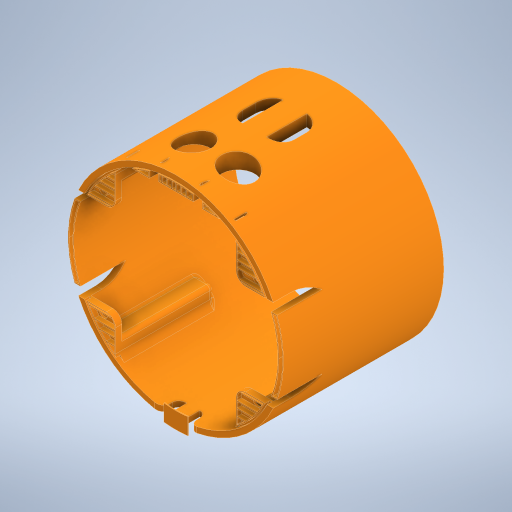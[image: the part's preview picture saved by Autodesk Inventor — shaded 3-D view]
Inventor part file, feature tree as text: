
AUTODESK INVENTOR PART (.ipt)
format: ipt  version: 2023 (Build 270158000, 158)  size: 1,089,536 bytes
history: native  units: mm
features: extrude x19, projected_geometry x15, sketch x13, fillet x10, mirror x5, plane x3, other x1
ambient origin geometry x8: Origin, YZ Plane, XZ Plane, XY Plane, X Axis, Y Axis, Z Axis, Center Point
bodies: Body1 (feature_tree)
feature tree (66):
  other  "Sólido1"
  extrude  "Extrusión1"  Depth=3.0mm
  extrude  "Extrusión2"  Depth=18.0mm
  extrude  "Extrusión3"  Depth=9.0mm
  extrude  "Extrusión4"  Depth=2.5mm TaperAngle=0.0deg
  sketch  "Boceto3"  dims[d3=50.0mm d4=18.0mm]
  extrude  "Extrusión5"  Depth=7.0mm TaperAngle=0.0deg
  fillet  "Empalme1"  Radius=7.0mm
  fillet  "Empalme2"  Radius=25.0mm
  fillet  "Empalme3"  Radius=53.0mm
  fillet  "Empalme4"  Radius=25.0mm
  fillet  "Empalme5"  Radius=1.0mm
  fillet  "Empalme6"  Radius=20.0mm
  fillet  "Empalme7"  Radius=4.0mm
  fillet  "Empalme8"  Radius=4.0mm
  sketch  "Boceto4"  dims[d5=4.5mm d8=9.0mm]
  extrude  "Extrusión6"  Depth=5.0mm
  extrude  "Extrusión7"  Depth=5.0mm
  extrude  "Extrusión8"  Depth=12.5mm
  sketch  "Boceto5"  dims[d9=15.0mm d10=2.5mm d11=0.0mm]
  extrude  "Extrusión9"  Depth=45.0mm
  fillet  "Empalme9"  Radius=2.0mm
  extrude  "Extrusión10"  Depth=18.0mm
  extrude  "Extrusión11"  Depth=2.5mm TaperAngle=0.0deg
  extrude  "Extrusión12"  Depth=35.0mm TaperAngle=0.0deg
  extrude  "Extrusión13"  Depth=10.0mm
  extrude  "Extrusión14"  Depth=10.0mm
  mirror  "Simetría1"
  mirror  "Simetría2"
  extrude  "Extrusión15"  Depth=10.0mm TaperAngle=0.0deg
  extrude  "Extrusión16"  Depth=10.0mm
  extrude  "Extrusión17"  Depth=10.0mm
  extrude  "Extrusión18"  Depth=10.0mm
  fillet  "Empalme11"  Radius=15.0mm
  mirror  "Simetría3"
  mirror  "Simetría4"
  extrude  "Extrusión19"  Depth=10.0mm
  mirror  "Simetría5"
  sketch  "Boceto2"  dims[d0=111.5mm d1=3.0mm]
  projected_geometry  "Contorno proyectado1"
  projected_geometry  "Contorno proyectado2"
  projected_geometry  "Contorno proyectado3"
  sketch  "Boceto6"  dims[d12=60.0mm d13=1.0mm d14=0.0mm d15=7.0mm d16=0.0mm d18=25.0mm d19=0.0mm d20=53.0mm d21=0.0mm d22=25.0mm d23=1.0mm d24=20.0mm d25=4.0mm d26=4.0mm]
  projected_geometry  "Contorno proyectado4"
  sketch  "Boceto7"  dims[d27=50.0mm d28=5.0mm]
  projected_geometry  "Contorno proyectado5"
  projected_geometry  "Contorno proyectado6"
  sketch  "Boceto8"  dims[d29=5.0mm d30=5.0mm]
  projected_geometry  "Contorno proyectado7"
  sketch  "Boceto9"  dims[d31=5.0mm d32=12.5mm]
  projected_geometry  "Contorno proyectado8"
  plane  "Plano de trabajo1"
  plane  "Plano de trabajo2"
  plane  "Plano de trabajo3"
  sketch  "Boceto10"  dims[d33=21.0mm d34=45.0mm d35=2.0mm]
  projected_geometry  "Contorno proyectado9"
  sketch  "Boceto11"  dims[d36=24.0mm d37=18.0mm]
  projected_geometry  "Contorno proyectado10"
  sketch  "Boceto12"  dims[d38=12.0mm d39=2.5mm d40=0.0mm]
  projected_geometry  "Contorno proyectado11"
  projected_geometry  "Contorno proyectado12"
  sketch  "Boceto13"  dims[d41=40.0mm d42=35.0mm d43=0.0mm]
  projected_geometry  "Contorno proyectado13"
  sketch  "Boceto14"  dims[d44=1.0mm d45=8.25mm d46=20.5mm d47=0.5mm d48=0.0mm d49=8.75mm d50=20.5mm d51=32.0mm d52=15.0mm d53=28.0mm d54=22.0mm d55=6.0mm d56=0.5mm d57=0.0mm d58=7.5mm d59=1.0mm d60=27.25mm d61=2.0mm d62=0.5mm d63=0.0mm d65=0.5mm d66=51.0mm d67=0.0mm d68=0.5mm d69=0.5mm d70=0.0mm d71=0.0mm d72=0.5mm d73=10.0mm d74=0.0mm d75=0.0mm d76=0.5mm d77=0.5mm d78=0.5mm d81=0.5mm d82=0.5mm d83=10.0mm d84=0.0mm d85=0.0mm d86=0.5mm d87=0.5mm d88=0.5mm d89=2.0mm d90=0.5mm d91=2.5mm d92=0.5mm d93=0.5mm d94=0.5mm d95=2.5mm d96=2.0mm d97=2.0mm d98=10.0mm d99=0.0mm d100=0.5mm d101=0.5mm d102=0.5mm d103=3.5mm d104=1.0mm d105=3.5mm d106=0.5mm d107=0.5mm d108=3.0mm d109=0.5mm d110=0.0mm d111=0.5mm d112=0.5mm d113=0.5mm d114=0.0mm d115=0.5mm d116=110.0mm d117=41.91mm d119=57.92mm d120=83.82mm d121=26.04mm d122=50.0mm d123=0.0mm d124=2.0mm d125=40.0mm d126=0.5mm d127=0.5mm d128=0.5mm d129=37.5mm d130=0.0mm]
  projected_geometry  "Contorno proyectado14"
  projected_geometry  "Contorno proyectado15"
